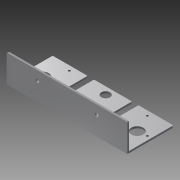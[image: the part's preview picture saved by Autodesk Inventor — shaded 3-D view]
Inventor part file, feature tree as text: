
AUTODESK INVENTOR PART (.ipt)
format: ipt  version: 2015 (Build 190159000, 159)  size: 203,776 bytes
history: native  units: mm
features: extrude x10, sketch x10, fillet x3, hole x2
ambient origin geometry x8: Origin, YZ Plane, XZ Plane, XY Plane, X Axis, Y Axis, Z Axis, Center Point
bodies: Solid1 (feature_tree)
feature tree (25):
  extrude  "Extrusion1"  Depth=7.0mm
  sketch  "Sketch2"  dims[d18=7.0mm]
  hole  "Hole1"  [1 undecoded]
  hole  "Hole2"  [1 undecoded]
  extrude  "Extrusion3"  Depth=3.5mm
  extrude  "Extrusion4"  Depth=7.0mm
  extrude  "Extrusion6"  Depth=2.0mm
  extrude  "Extrusion7"  TaperAngle=180.0deg  [1 undecoded]
  extrude  "Extrusion8"  Depth=50.0mm
  extrude  "Extrusion9"  Depth=2.0mm
  fillet  "Fillet1"  Radius=2.4mm
  fillet  "Fillet2"  Radius=2.4mm
  extrude  "Extrusion10"  Depth=2.0mm
  extrude  "Extrusion11"  Depth=2.0mm TaperAngle=0.0deg
  fillet  "Fillet3"  Radius=2.0mm
  extrude  "Extrusion12"  Depth=2.0mm TaperAngle=0.0deg
  sketch  "Sketch1"  dims[d11=131.0mm d12=0.0mm d17=7.0mm]
  sketch  "Sketch3"  dims[d19=7.0mm d20=6.0mm d21=4.0mm d22=2.0mm d23=90.0deg d24=2.0mm d25=0.0mm d26=51.3mm]
  sketch  "Sketch7"  dims[d27=51.3mm d28=19.0mm]
  sketch  "Sketch8"  dims[d29=3.5mm d30=3.5mm]
  sketch  "Sketch9"  dims[d31=3.5mm d32=6.0mm d33=4.0mm d34=2.0mm d35=90.0deg d36=2.0mm d37=0.0mm d89=7.0mm]
  sketch  "Sketch11"  dims[d90=2.0mm d91=0.0mm d96=31.0mm]
  sketch  "Sketch12"  dims[d97=25.0mm d98=180.0deg]
  sketch  "Sketch14"  dims[d99=50.0mm d100=2.4mm]
  sketch  "Sketch15"  dims[d101=2.4mm d104=2.4mm d105=2.4mm d106=2.4mm d107=2.4mm d108=2.0mm d109=0.0mm d112=2.0mm d113=0.0mm d114=2.0mm d115=0.0mm d116=13.0mm d117=13.0mm d118=2.0mm d119=0.0mm d125=2.0mm d126=0.0mm d127=1.0mm d128=1.0mm d129=8.0mm d130=9.5mm d131=2.0mm d132=0.0mm d133=18.0mm d134=0.0mm d135=1.0mm d139=4.0mm d140=4.0mm d141=2.0mm d142=0.0mm]
note: 3 required parameter values undecoded (feature->parameter linkage not recoverable at this tier; creation-order binding heuristic only, values carry confidence <= 0.55)
